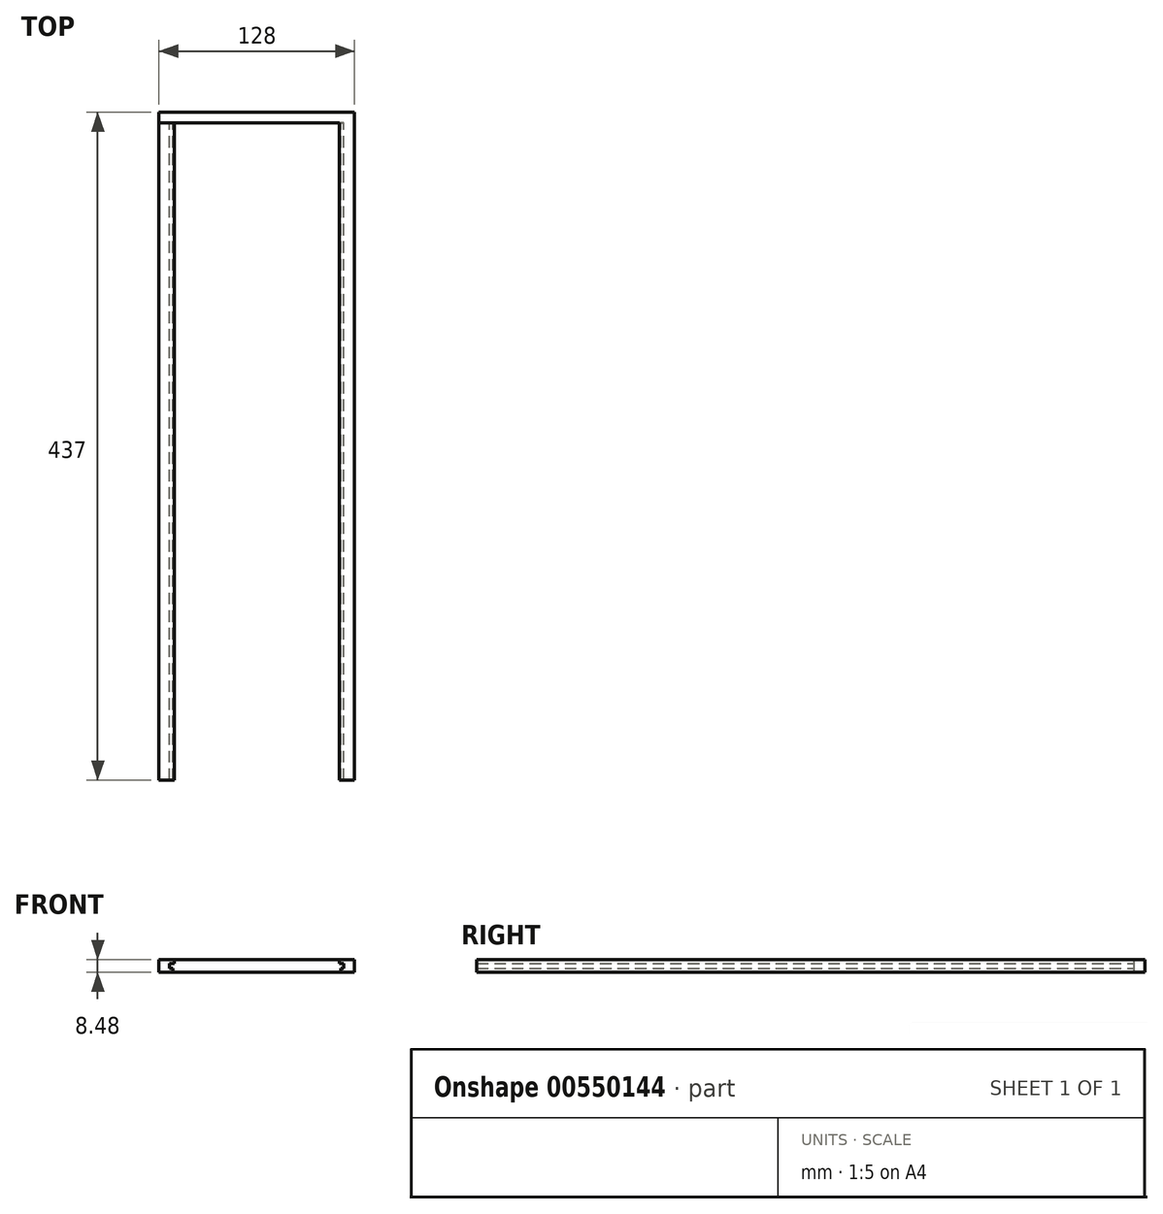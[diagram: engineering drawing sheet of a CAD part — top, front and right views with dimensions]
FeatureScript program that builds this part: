
annotation { "Feature Type Name" : "Feature", "Feature Type Description" : "" }
export const myFeature = defineFeature(function(context is Context, id is Id, definition is map)
    precondition{}
    {
        {
            var Q0;
            Q0=qCreatedBy(makeId("Front.planeOp"),FACE);
            var sketch = newSketch(context, id + "F0", { "sketchPlane" : qUnion([Q0])});
            skLineSegment(sketch, "E0", {"start": v(-57.44, 39) * mm, "end": v(-47.44, 39) * mm});
            skLineSegment(sketch, "E1", {"start": v(-47.44, 39) * mm, "end": v(-47.44, 30.6) * mm});
            skLineSegment(sketch, "E2", {"start": v(-47.44, 30.6) * mm, "end": v(-56.44, 30.6) * mm});
            skLineSegment(sketch, "E3", {"start": v(-56.44, 30.6) * mm, "end": v(-56.44, 33.1) * mm});
            skLineSegment(sketch, "E4", {"start": v(-56.44, 33.1) * mm, "end": v(-54.44, 33.1) * mm});
            skLineSegment(sketch, "E5", {"start": v(-54.44, 33.1) * mm, "end": v(-54.44, 36.5) * mm});
            skLineSegment(sketch, "E6", {"start": v(-54.44, 36.5) * mm, "end": v(-57.44, 36.5) * mm});
            skLineSegment(sketch, "E7", {"start": v(-57.44, 36.5) * mm, "end": v(-57.44, 39) * mm});
            skSolve(sketch);
        }
        {
            var Q0;
            Q0 = qSketchRegion(id + "F0", true);
            extrude(context, id + "F1", {"entities" : qUnion([Q0]), "depth" : 430 * mm, "offsetDistance" : 25 * mm});
        }
        {
            var Q0;
            Q0=qCreatedBy(makeId("Front.planeOp"),FACE);
            var sketch = newSketch(context, id + "F2", { "sketchPlane" : qUnion([Q0])});
            skLineSegment(sketch, "E8.bottom", {"start": v(-175.44, 39) * mm, "end": v(-47.44, 39) * mm});
            skLineSegment(sketch, "E8.top", {"start": v(-175.44, 30.6) * mm, "end": v(-47.44, 30.6) * mm});
            skLineSegment(sketch, "E8.left", {"start": v(-175.44, 39) * mm, "end": v(-175.44, 30.6) * mm});
            skLineSegment(sketch, "E8.right", {"start": v(-47.44, 39) * mm, "end": v(-47.44, 30.6) * mm});
            skSolve(sketch);
        }
        {
            var Q0;
            Q0=makeQuery(id+"F2.imprint","IMPRINT",FACE,{"disambiguationData":[TD([[makeQuery(id+"F2.imprint","IMPRINT",EDGE,{"derivedFrom":sQuery(id+"F2.wireOp",EDGE,"E8.bottom")}),-1.0]])]});
            extrude(context, id + "F3", {"entities" : qUnion([Q0]), "operationType" : NewBodyOperationType.ADD, "oppositeDirection" : true, "depth" : 7 * mm, "offsetDistance" : 25 * mm});
        }
        {
            var Q0;
            Q0=qCreatedBy(makeId("Front.planeOp"),FACE);
            var sketch = newSketch(context, id + "F4", { "sketchPlane" : qUnion([Q0])});
            skLineSegment(sketch, "E9.MirrorCS", {"start": v(-165.44, 39.07) * mm, "end": v(-175.44, 39.07) * mm});
            skLineSegment(sketch, "E10.MirrorCS", {"start": v(-175.44, 39.07) * mm, "end": v(-175.44, 30.67) * mm});
            skLineSegment(sketch, "E11.MirrorCS", {"start": v(-175.44, 30.67) * mm, "end": v(-166.44, 30.67) * mm});
            skLineSegment(sketch, "E12.MirrorCS", {"start": v(-166.44, 30.67) * mm, "end": v(-166.44, 33.17) * mm});
            skLineSegment(sketch, "E13.MirrorCS", {"start": v(-166.44, 33.17) * mm, "end": v(-168.44, 33.17) * mm});
            skLineSegment(sketch, "E14.MirrorCS", {"start": v(-168.44, 33.17) * mm, "end": v(-168.44, 36.57) * mm});
            skLineSegment(sketch, "E15.MirrorCS", {"start": v(-168.44, 36.57) * mm, "end": v(-165.44, 36.57) * mm});
            skLineSegment(sketch, "E16.MirrorCS", {"start": v(-165.44, 36.57) * mm, "end": v(-165.44, 39.07) * mm});
            skSolve(sketch);
        }
        {
            var Q0;
            Q0 = qSketchRegion(id + "F4", true);
            extrude(context, id + "F5", {"entities" : qUnion([Q0]), "operationType" : NewBodyOperationType.ADD, "depth" : 430 * mm, "offsetDistance" : 25 * mm});
        }
    });
